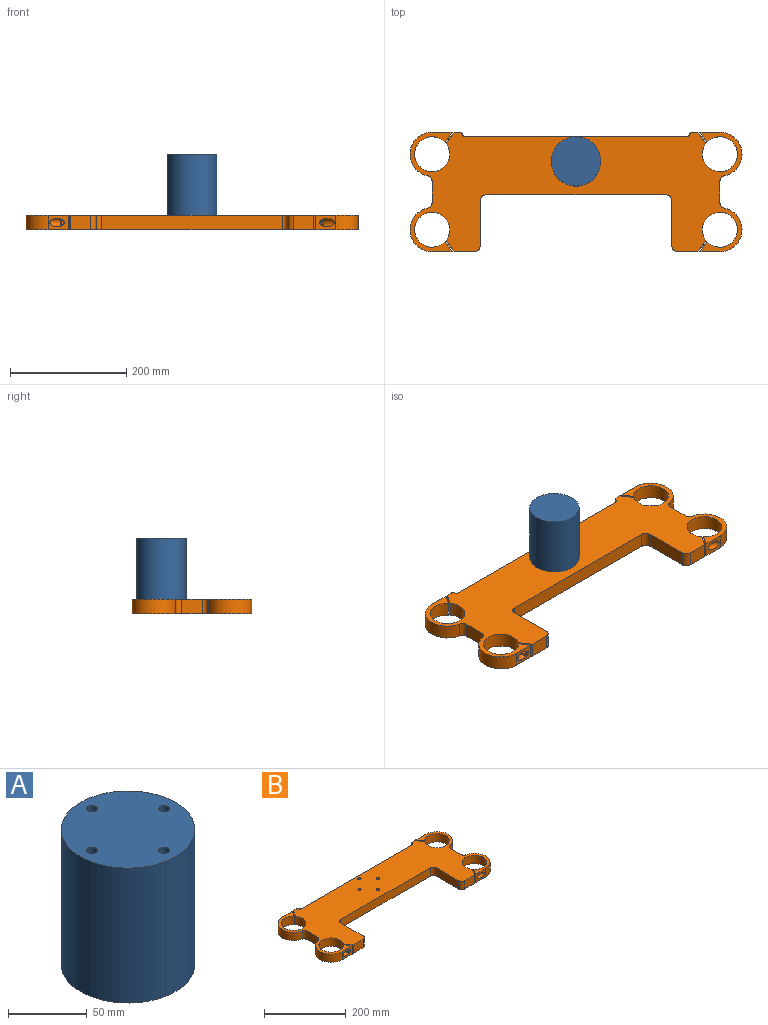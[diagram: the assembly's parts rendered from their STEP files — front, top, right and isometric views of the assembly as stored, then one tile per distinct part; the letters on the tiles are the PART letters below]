
ASSEMBLY  parts=2 mates=1
PART A: 11 faces, bbox 85x85x105 mm
  f0: cylinder r=42.5mm len=105mm, axis (0,0,-1), area 28038.7mm2, adj f1,f2
  f1: plane 85x85mm, normal (0,0,1), area 5529.2mm2, adj f0,f4,f6,f8,f10
  f2: plane 85x85mm, normal (0,0,-1), area 5674.5mm2, adj f0
  f3: cone r=0mm half-angle=59deg, axis (0,0,1), area 42.4mm2, adj f4
  f4: cylinder r=3.4mm len=25mm, axis (0,0,1), area 534.1mm2, adj f1,f3
  f5: cone r=0mm half-angle=59deg, axis (0,0,1), area 42.4mm2, adj f6
  f6: cylinder r=3.4mm len=25mm, axis (0,0,1), area 534.1mm2, adj f1,f5
  f7: cone r=0mm half-angle=59deg, axis (0,0,1), area 42.4mm2, adj f8
  f8: cylinder r=3.4mm len=25mm, axis (0,0,1), area 534.1mm2, adj f1,f7
  f9: cone r=0mm half-angle=59deg, axis (0,0,1), area 42.4mm2, adj f10
  f10: cylinder r=3.4mm len=25mm, axis (0,0,1), area 534.1mm2, adj f1,f9
PART B: 68 faces, bbox 571x229.6x25 mm
  f0: plane 25x20.26mm, normal (-0.83,-0.56,0), area 576.6mm2, adj f1,f45,f46,f47,f56
  f1: plane 34.5x25mm, normal (0,-1,0), area 862.5mm2, adj f0,f2,f46,f47
  f2: cylinder r=10mm len=25mm, axis (0,0,-1), area 392.7mm2, adj f1,f3,f46,f47
  f3: plane 78x25mm, normal (1,0,0), area 1950mm2, adj f2,f4,f46,f47
  f4: cylinder r=10mm len=25mm, axis (0,0,-1), area 392.7mm2, adj f3,f5,f46,f47
  f5: plane 310x25mm, normal (0,-1,0), area 7750mm2, adj f4,f6,f46,f47
  f6: cylinder r=10mm len=25mm, axis (0,0,-1), area 392.7mm2, adj f5,f7,f46,f47
  f7: plane 78x25mm, normal (-1,0,0), area 1950mm2, adj f6,f8,f46,f47
  f8: cylinder r=10mm len=25mm, axis (0,0,-1), area 392.7mm2, adj f7,f9,f46,f47
  f9: plane 34.5x25mm, normal (0,-1,0), area 862.5mm2, adj f8,f10,f46,f47
  f10: plane 25x20.26mm, normal (0.83,-0.56,0), area 576.6mm2, adj f9,f11,f46,f47,f51
  f11: cylinder r=30mm len=60mm, axis (0,0,-1), area 4634.1mm2, adj f10,f12,f46,f47
  f12: plane 25x17.83mm, normal (-0.83,0.56,0), area 503.3mm2, adj f11,f13,f46,f47,f48
  f13: plane 34.37x25mm, normal (0,-1,0), area 576.1mm2, adj f12,f14,f46,f47,f50
  f14: cylinder r=38mm len=75.17mm, axis (0,0,-1), area 2785.1mm2, adj f13,f15,f46,f47
  f15: cylinder r=10mm len=25mm, axis (0,0,-1), area 340.2mm2, adj f14,f16,f46,f47
  f16: plane 36.11x25mm, normal (1,0,0), area 902.7mm2, adj f15,f17,f46,f47
  f17: cylinder r=10mm len=25mm, axis (0,0,-1), area 340.2mm2, adj f16,f18,f46,f47
  f18: cylinder r=38mm len=75.17mm, axis (0,0,-1), area 2785.1mm2, adj f17,f19,f46,f47
  f19: plane 34.37x25mm, normal (0,1,0), area 576.1mm2, adj f18,f20,f46,f47,f62
  f20: plane 25x17.83mm, normal (-0.83,-0.56,0), area 503.3mm2, adj f19,f21,f46,f47,f60
  f21: cylinder r=30mm len=60mm, axis (0,0,-1), area 4634.1mm2, adj f20,f22,f46,f47
  f22: plane 25x20.26mm, normal (0.83,0.56,0), area 576.6mm2, adj f21,f23,f46,f47,f59
  f23: plane 25x9.28mm, normal (0,1,0), area 232mm2, adj f22,f24,f46,f47
  f24: cylinder r=5mm len=25mm, axis (0,0,-1), area 171.2mm2, adj f23,f25,f46,f47
  f25: cylinder r=5mm len=25mm, axis (0,0,-1), area 171.2mm2, adj f24,f26,f46,f47
  f26: plane 380.85x25mm, normal (0,1,0), area 9521.1mm2, adj f25,f27,f46,f47
  f27: cylinder r=5mm len=25mm, axis (0,0,-1), area 171.2mm2, adj f26,f28,f46,f47
  f28: cylinder r=5mm len=25mm, axis (0,0,-1), area 171.2mm2, adj f27,f29,f46,f47
  f29: plane 25x9.28mm, normal (0,1,0), area 232mm2, adj f28,f30,f46,f47
  f30: plane 25x20.26mm, normal (-0.83,0.56,0), area 576.6mm2, adj f29,f31,f46,f47,f66
  f31: cylinder r=30mm len=60mm, axis (0,0,-1), area 4634.1mm2, adj f30,f32,f46,f47
  f32: plane 25x17.83mm, normal (0.83,-0.56,0), area 503.3mm2, adj f31,f33,f46,f47,f63
  f33: plane 34.37x25mm, normal (0,1,0), area 576.1mm2, adj f32,f34,f46,f47,f65
  f34: cylinder r=38mm len=75.17mm, axis (0,0,-1), area 2785.1mm2, adj f33,f35,f46,f47
  f35: cylinder r=10mm len=25mm, axis (0,0,-1), area 340.2mm2, adj f34,f36,f46,f47
  f36: plane 36.11x25mm, normal (-1,0,0), area 902.7mm2, adj f35,f37,f46,f47
  f37: cylinder r=10mm len=25mm, axis (0,0,-1), area 340.2mm2, adj f36,f38,f46,f47
  f38: cylinder r=38mm len=75.17mm, axis (0,0,-1), area 2785.1mm2, adj f37,f39,f46,f47
  f39: plane 34.37x25mm, normal (0,-1,0), area 576.1mm2, adj f38,f40,f46,f47,f53
  f40: plane 25x17.83mm, normal (0.83,0.56,0), area 503.3mm2, adj f39,f45,f46,f47,f55
  f41: cylinder r=4.1mm len=25mm, axis (0,0,-1), area 644mm2, adj f46,f47
  f42: cylinder r=4.1mm len=25mm, axis (0,0,-1), area 644mm2, adj f46,f47
  f43: cylinder r=4.1mm len=25mm, axis (0,0,-1), area 644mm2, adj f46,f47
  f44: cylinder r=4.1mm len=25mm, axis (0,0,-1), area 644mm2, adj f46,f47
  f45: cylinder r=30mm len=60mm, axis (0,0,-1), area 4634.1mm2, adj f0,f40,f46,f47
  f46: plane 571x206mm, normal (0,0,1), area 63841.2mm2, adj f0,f1,f2,f3,f4,f5,f6,f7
  f47: plane 571x206mm, normal (0,0,-1), area 63841.2mm2, adj f0,f1,f2,f3,f4,f5,f6,f7
  f48: cylinder r=3.4mm len=8.05mm, axis (0.83,-0.56,0), area 92.1mm2, adj f12,f49
  f49: plane 14.25x11.77mm, normal (0.83,-0.56,0), area 123.2mm2, adj f48,f50
  f50: cylinder r=7.12mm len=26.13mm, axis (0.83,-0.56,0), area 512.6mm2, adj f13,f49
  f51: cylinder r=3.4mm len=17.62mm, axis (0.83,-0.56,0), area 356.5mm2, adj f10,f52
  f52: cone r=0mm half-angle=59deg, axis (0.83,-0.56,0), area 42.4mm2, adj f51
  f53: cylinder r=7.12mm len=26.12mm, axis (-0.83,-0.56,0), area 512.6mm2, adj f39,f54
  f54: plane 14.25x11.77mm, normal (-0.83,-0.56,0), area 123.2mm2, adj f53,f55
  f55: cylinder r=3.4mm len=8.05mm, axis (-0.83,-0.56,0), area 92.1mm2, adj f40,f54
  f56: cylinder r=3.4mm len=17.62mm, axis (-0.83,-0.56,0), area 356.5mm2, adj f0,f57
  f57: cone r=0mm half-angle=59deg, axis (-0.83,-0.56,0), area 42.4mm2, adj f56
  f58: cone r=0mm half-angle=59deg, axis (0.83,0.56,0), area 42.4mm2, adj f59
  f59: cylinder r=3.4mm len=17.62mm, axis (0.83,0.56,0), area 356.5mm2, adj f22,f58
  f60: cylinder r=3.4mm len=8.05mm, axis (0.83,0.56,0), area 92.1mm2, adj f20,f61
  f61: plane 14.25x11.77mm, normal (0.83,0.56,0), area 123.2mm2, adj f60,f62
  f62: cylinder r=7.12mm len=26.12mm, axis (0.83,0.56,0), area 512.6mm2, adj f19,f61
  f63: cylinder r=3.4mm len=8.05mm, axis (-0.83,0.56,0), area 92.1mm2, adj f32,f64
  f64: plane 14.25x11.77mm, normal (-0.83,0.56,0), area 123.2mm2, adj f63,f65
  f65: cylinder r=7.12mm len=26.13mm, axis (-0.83,0.56,0), area 512.6mm2, adj f33,f64
  f66: cylinder r=3.4mm len=17.62mm, axis (-0.83,0.56,0), area 356.5mm2, adj f30,f67
  f67: cone r=0mm half-angle=59deg, axis (-0.83,0.56,0), area 42.4mm2, adj f66
PLACE A rot(axis=(1,0,0),180deg) t=(-18.74,39.59,274.31)mm
PLACE B t=(-18.74,-12.91,156.81)mm
MATE fastened A.f9 <-> B.f43  axis (0,0,-1) through (-18.74,7.09,169.31)mm
